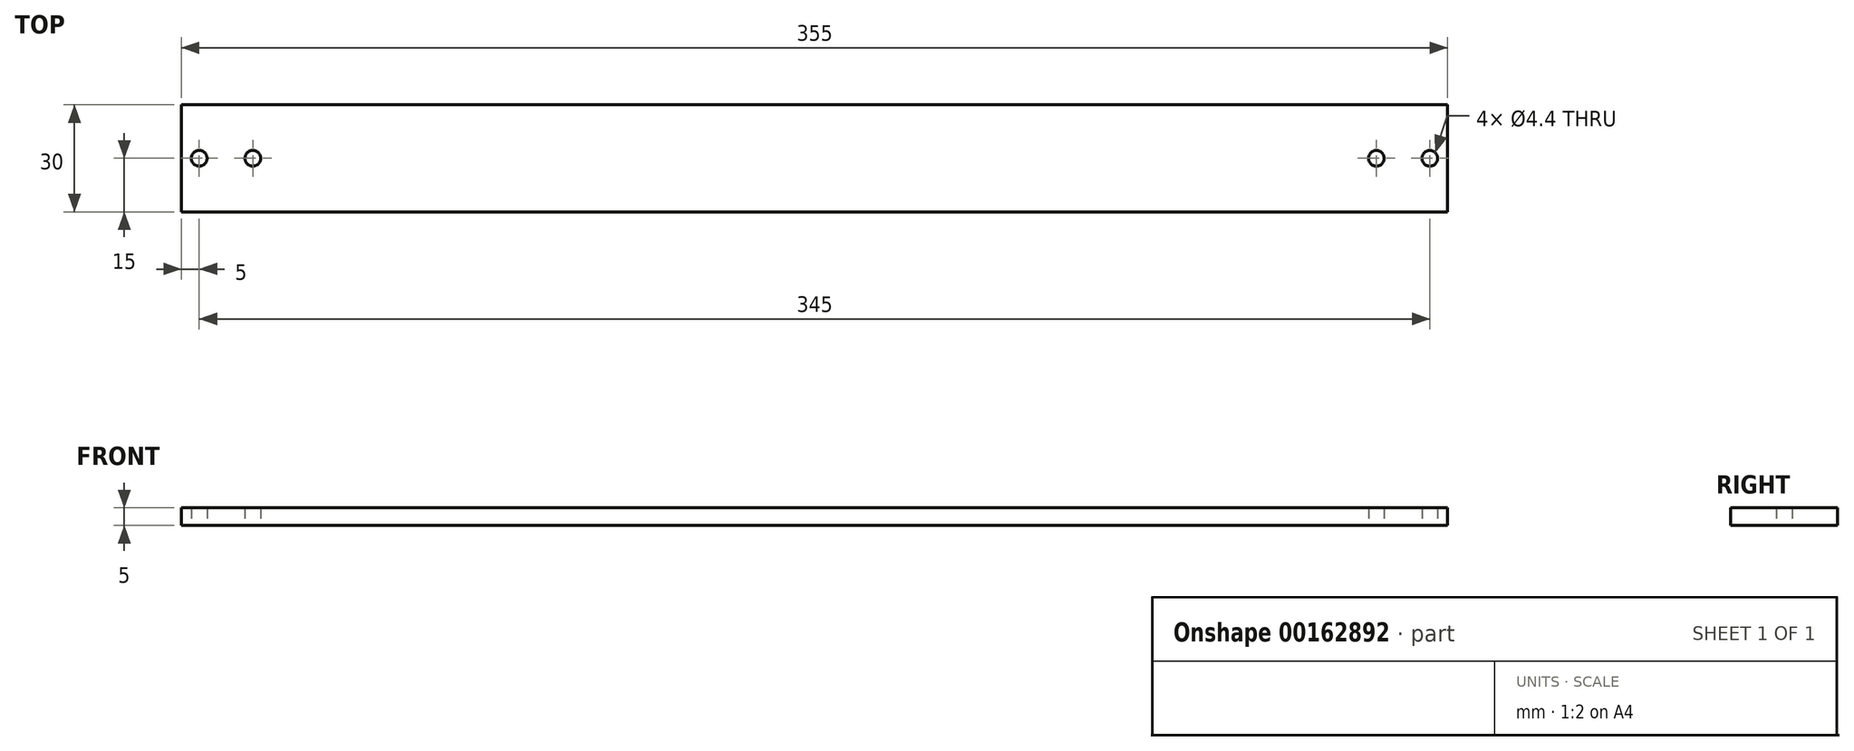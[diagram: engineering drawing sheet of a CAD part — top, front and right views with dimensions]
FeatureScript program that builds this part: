
annotation { "Feature Type Name" : "Feature", "Feature Type Description" : "" }
export const myFeature = defineFeature(function(context is Context, id is Id, definition is map)
    precondition{}
    {
        {
            var Q0;
            Q0=qCreatedBy(makeId("Top.planeOp"),FACE);
            var sketch = newSketch(context, id + "F0", { "sketchPlane" : qUnion([Q0])});
            skLineSegment(sketch, "E0.bottom", {"start": v(177.5, -15) * mm, "end": v(-177.5, -15) * mm});
            skLineSegment(sketch, "E0.top", {"start": v(177.5, 15) * mm, "end": v(-177.5, 15) * mm});
            skLineSegment(sketch, "E0.left", {"start": v(177.5, -15) * mm, "end": v(177.5, 15) * mm});
            skLineSegment(sketch, "E0.right", {"start": v(-177.5, -15) * mm, "end": v(-177.5, 15) * mm});
            skPoint(sketch, "E0.middle", {"position": v(0, 0) * mm});
            skPoint(sketch, "E1", {"position": v(-172.5, 0) * mm});
            skPoint(sketch, "E1.positionSnap0", {"position": v(-177.5, 0) * mm});
            skPoint(sketch, "E2", {"position": v(-157.5, 0) * mm});
            skPoint(sketch, "E3.MirrorP", {"position": v(157.5, 0) * mm});
            skPoint(sketch, "E4.MirrorP", {"position": v(172.5, 0) * mm});
            skSolve(sketch);
        }
        {
            var Q0;
            Q0=makeQuery(id+"F0.imprint","IMPRINT",FACE,{"disambiguationData":[TD([[makeQuery(id+"F0.imprint","IMPRINT",EDGE,{"derivedFrom":sQuery(id+"F0.wireOp",EDGE,"E0.bottom")}),-1.0]])]});
            extrude(context, id + "F1", {"entities" : qUnion([Q0]), "depth" : 5 * mm, "offsetDistance" : 25 * mm});
        }
        {
            var Q0;
            Q0=sQuery(id+"F0.wireOp",VERTEX,"E3.MirrorP");
            var Q1;
            Q1=sQuery(id+"F0.wireOp",VERTEX,"E4.MirrorP");
            var Q2;
            Q2=sQuery(id+"F0.wireOp",VERTEX,"E2");
            var Q3;
            Q3=sQuery(id+"F0.wireOp",VERTEX,"E1");
            var Q4;
            Q4=makeQuery(id+"F1.opExtrude","SWEPT_BODY",BODY,{"disambiguationData":[OSD([sQuery(id+"F0.wireOp",EDGE,"E0.bottom"),sQuery(id+"F0.wireOp",EDGE,"E0.top"),sQuery(id+"F0.wireOp",EDGE,"E0.left"),sQuery(id+"F0.wireOp",EDGE,"E0.right")])]});
            hole(context, id + "F2", {"style" : HoleStyle.SIMPLE, "endStyle" : HoleEndStyle.THROUGH, "oppositeDirection" : true, "standardTappedOrClearance" : lookupTablePath({ "standard" : "ISO", "fit" : "Normal", "size" : "M4", "type" : "Clearance" }), "standardBlindInLast" : lookupTablePath({ "fit" : "Standard", "standard" : "ISO", "size" : "M4", "type" : "Clearance" }), "holeDiameter" : 4.4 * mm, "majorDiameter" : 5 * mm, "isTappedThrough" : true, "tappedDepth" : 12 * mm, "tapClearance" : 3, "startFromSketch" : true, "locations" : qUnion([Q0, Q1, Q2, Q3]), "scope" : qUnion([Q4])});
        }
    });
